# Revit family: Building-IEC309Boards-GEWISS-68QDIN-DISTRIBUTION-BOARD-5MOD_2SOCKET-OUTLETS-16A
name_source: partatom
category: Apparecchi elettrici
units: mm (PartAtom-declared; Revit-internal decimal feet)

## family parameters
Condiviso = No
Host = Superficie
Mantenere orientamento annotazione = Sì
Punto di calcolo locali = Sì
Quota connettore circolare = Usa diametro
Taglio con vuoti quando caricato = No
Tipo di parte = Normale

## types (1)
- GW68018N - Q-DIN 5M 2 FLANGES S.O.16A IP65
    Accordance with Standards = EN 62208
    Catalogue = BUILDING
    Colour = Grey RAL 7035
    Descrizione = Q-DIN 5M 2 FLANGES S.O.16A IP65
    Dispersible power A (W) = 10
    Dispersible power B (W) = 37
    Electrocod = 2242
    Glow Wire Test = 650°C
    Houseable socket = 2 IEC 309 16A IP44/67
    IDF = 20c9f9c3-1f44-44a2-bc85-bb1be325a016
    IDT = 7f2f8e9d144b46a0836ce811937ca44a
    IP degree = IP65
    Immagine tipo = GW68018N.jpg
    Installation type = Surface-mounting
    Insulation class = II
    L_moduli = 95 mm  [stored 0.31168 ft]
    Modello = GW68018N
    N_moduli = 5 mm  [stored 0.0164042 ft]
    No. of modules EN 50022 = 5
    No. of provided blank lids = -
    Operating temperature: = -25 +40 °C
    POMELLO = bianco
    PRESA = rosso
    Produttore = GEWISS S.p.A.
    Prospetto di default = 1219 mm
    SEO = Board
    STRUTTURA = RAL - 7035
    STRUTTURA ALTA = Poche
    Shock resistance = IK08
    Spostamento_S = 1000 mm  [stored 3.28084 ft]
    Technical sheet = https://www.gewiss.com
    Thermo-pressure with ball = 70
    URL = https://www.gewiss.com
    VETRO = Vetro
    Version file RFA = 21.5
    Version type = Empty

note: source unit labels omitted for Thermo-pressure with ball — the stored unit's dimension contradicts the parameter name (converter mislabeling)

note: [stored X ft] marks values corroborated as IEEE doubles in the binary element streams (Revit-internal decimal feet)

## geometry (parser evidence)
native form markers: Sweep x8
no freeform markers — native parametric forms only
